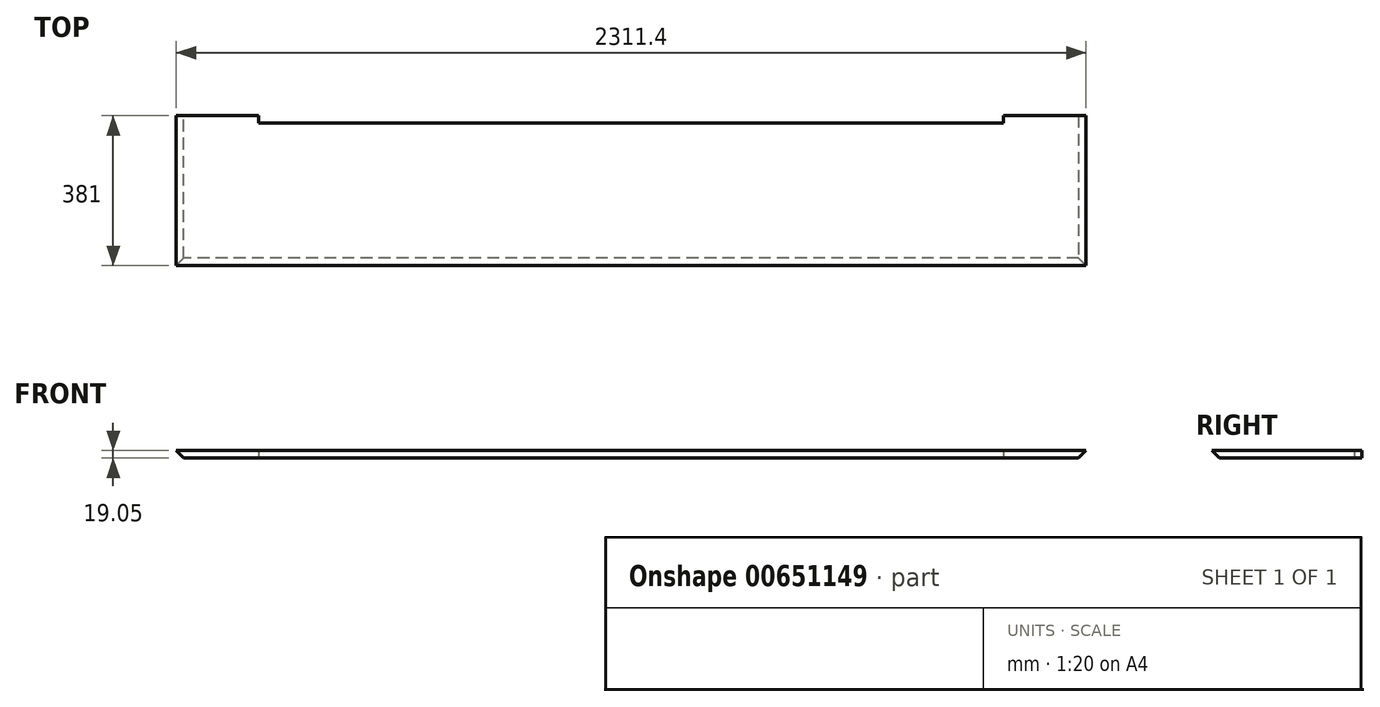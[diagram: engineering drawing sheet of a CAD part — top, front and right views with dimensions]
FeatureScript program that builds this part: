
annotation { "Feature Type Name" : "Feature", "Feature Type Description" : "" }
export const myFeature = defineFeature(function(context is Context, id is Id, definition is map)
    precondition{}
    {
        {
            var Q0;
            Q0=qCreatedBy(makeId("Top.planeOp"),FACE);
            var sketch = newSketch(context, id + "F0", { "sketchPlane" : qUnion([Q0])});
            skLineSegment(sketch, "E0.top", {"start": v(1155.7, -190.5) * mm, "end": v(-1155.7, -190.5) * mm});
            skLineSegment(sketch, "E0.right", {"start": v(-1155.7, 190.5) * mm, "end": v(-1155.7, -190.5) * mm});
            skPoint(sketch, "E0.middle", {"position": v(0, 0) * mm});
            skLineSegment(sketch, "E1", {"start": v(-946.15, 171.45) * mm, "end": v(946.15, 171.45) * mm});
            skLineSegment(sketch, "E2.trimOffspring", {"start": v(-946.15, 190.5) * mm, "end": v(-1155.7, 190.5) * mm});
            skLineSegment(sketch, "E3", {"start": v(1155.7, -190.5) * mm, "end": v(1155.7, 190.5) * mm});
            skLineSegment(sketch, "E4", {"start": v(-946.15, 190.5) * mm, "end": v(-946.15, 171.45) * mm});
            skLineSegment(sketch, "E5.MirrorCS", {"start": v(946.15, 190.5) * mm, "end": v(946.15, 171.45) * mm});
            skLineSegment(sketch, "E6.MirrorCS", {"start": v(946.15, 190.5) * mm, "end": v(1155.7, 190.5) * mm});
            skSolve(sketch);
        }
        {
            var Q0;
            Q0=makeQuery(id+"F0.imprint","IMPRINT",FACE,{"disambiguationData":[TD([[makeQuery(id+"F0.imprint","IMPRINT",EDGE,{"derivedFrom":sQuery(id+"F0.wireOp",EDGE,"E0.top")}),-1.0]])]});
            extrude(context, id + "F1", {"entities" : qUnion([Q0]), "depth" : 19.05 * mm, "offsetDistance" : 25.4 * mm});
        }
        {
            var Q0;
            Q0=makeQuery(id+"F1.opExtrude","CAP_EDGE",EDGE,{"disambiguationData":[OSD([sQuery(id+"F0.wireOp",EDGE,"E0.right")])],"isStart":true});
            var Q1;
            Q1=makeQuery(id+"F1.opExtrude","CAP_EDGE",EDGE,{"disambiguationData":[OSD([sQuery(id+"F0.wireOp",EDGE,"E0.top")])],"isStart":true});
            var Q2;
            Q2=makeQuery(id+"F1.opExtrude","CAP_EDGE",EDGE,{"disambiguationData":[OSD([sQuery(id+"F0.wireOp",EDGE,"E3")])],"isStart":true});
            chamfer(context, id + "F2", {"entities" : qUnion([Q0, Q1, Q2]), "width" : 19.05 * mm, "tangentPropagation" : true});
        }
    });
